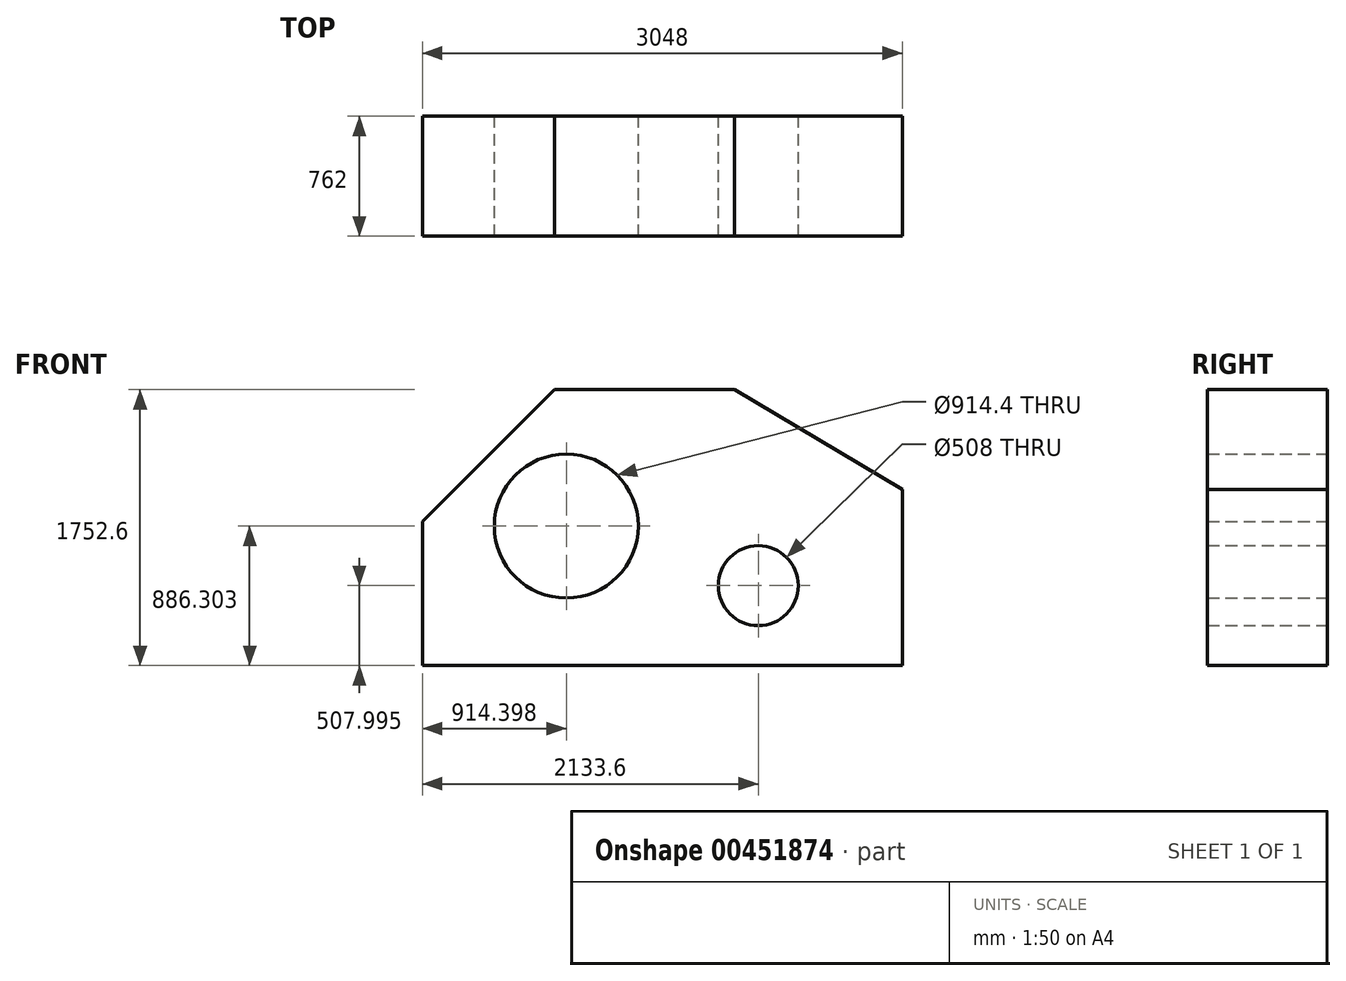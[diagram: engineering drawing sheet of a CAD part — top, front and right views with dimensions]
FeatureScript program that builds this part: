
annotation { "Feature Type Name" : "Feature", "Feature Type Description" : "" }
export const myFeature = defineFeature(function(context is Context, id is Id, definition is map)
    precondition{}
    {
        {
            var Q0;
            Q0=qCreatedBy(makeId("Front.planeOp"),FACE);
            var sketch = newSketch(context, id + "F0", { "sketchPlane" : qUnion([Q0])});
            skLineSegment(sketch, "E0", {"start": v(-111.05, -47.36) * mm, "end": v(2936.95, -47.36) * mm});
            skLineSegment(sketch, "E1", {"start": v(2936.95, -47.36) * mm, "end": v(2936.95, 1070.24) * mm});
            skLineSegment(sketch, "E2", {"start": v(2936.95, 1070.24) * mm, "end": v(1870.15, 1705.24) * mm});
            skLineSegment(sketch, "E3", {"start": v(1870.15, 1705.24) * mm, "end": v(727.15, 1705.24) * mm});
            skLineSegment(sketch, "E4", {"start": v(-111.05, -47.36) * mm, "end": v(-111.05, 867.04) * mm});
            skLineSegment(sketch, "E5", {"start": v(-111.05, 867.04) * mm, "end": v(727.15, 1705.24) * mm});
            skCircle(sketch, "E6", {"center": v(803.35, 838.94) * mm, "radius": 457.2 * mm});
            skCircle(sketch, "E7", {"center": v(2022.55, 460.64) * mm, "radius": 254 * mm});
            skPoint(sketch, "E7.centerSnap0", {"position": v(2936.95, 460.64) * mm});
            skSolve(sketch);
        }
        {
            var Q0;
            Q0=makeQuery(id+"F0.imprint","IMPRINT",FACE,{"disambiguationData":[TD([[makeQuery(id+"F0.imprint","IMPRINT",EDGE,{"derivedFrom":sQuery(id+"F0.wireOp",EDGE,"E0")}),1.0]])]});
            extrude(context, id + "F1", {"entities" : qUnion([Q0]), "depth" : 762 * mm});
        }
    });
